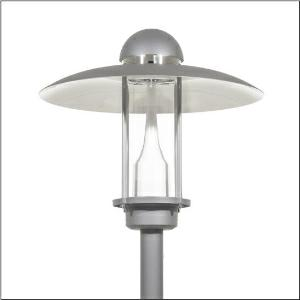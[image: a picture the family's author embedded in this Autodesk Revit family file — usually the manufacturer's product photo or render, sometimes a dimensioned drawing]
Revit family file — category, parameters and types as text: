
# Revit family: city-light_elegance_iq___pl1_2s_5xa5265of14h_1bea
name_source: partatom
category: Lighting Fixtures
units: mm (PartAtom-declared; Revit-internal decimal feet)

## family parameters
Cut with Voids When Loaded = No
Host = Face
Light Source = No
Part Type = Normal
Room Calculation Point = No
Round Connector Dimension = Use Diameter
Shared = No

## types (1)
- --- (1 x LED, 2840 lm, 21.8 W, 2700K)
    Apparent Load = 22 VA
    CIE Flux Codes = 24 63 94 98 100
    Color Rendering = 70
    Color Temperature = 2700K
    Default Elevation = 1800 mm
    Description = City-Light Elegance iQ, mast luminaire, Module 540 iQ-SR, primary light control with 3 zone facetted reflector, of plastic, silver coated, highly specular, structured, primary optical cover: cover, of PMMA, transparent, light distribution: PL1.2s, light emission: direct distribution, primary light characteristic: symmetric, installation type: post-top, LED, High Power LED, rated luminous flux: 2.840lm, luminous efficacy: 130lm/W, light colour: 727, colour temperature: 2700K, control gear: ECG iQ, control: presetting dimming logarithmic, Street-Remote, Auto-Match, Temp-Guard, Lumen-Switch, Night-Set, Smart-Wire, Light-Fading, Desk-Remote (wireless, voltage-free reading and setting of iQ features in the workshop via application-optimized NFC function/RFID function), optimised constant luminous flux control (CLO 2.0), with terminal, 6-pole, max. 2.5mm², mains connection: 230..240V, AC, 50/60Hz, start of lifetime: 22W, end of service life: 23W, reduction: 11W, luminaire housing, upper part, of aluminium, coated, Siteco® metallic grey (DB 702S), diameter: 750mm, height: 675mm, spigot size: d x l = 76 x 70mm (post-top) | with reducer (optional accessory) 60 x 70mm, post-top mast mounting element, of diecast aluminium, coated, Siteco® metallic grey (DB 702S), Module 540 iQ-SR, traffic white (RAL 9016), equipment: standard, protection rating (complete): IP65, insulation class (complete): insulation class II (safety insulation), certification: CE, ENEC, VDE, packaging unit: 1 piece

Light Distribution: PL1.2s
    Height = 675 mm
    Lamp = 1 x LED
    Lamp Light Flux = 2840 lm
    Lamp Power = 21.8 W
    Lamp count = 1
    Length = 750 mm
    Luminous efficacy = 130 lm/W
    Manufacturer = Siteco
    ModVariant = No
    Model = 5XA5265OF14H
    Number of Poles = 1
    OnlyDefault = Yes
    Power Factor = 1
    Product Name = City-Light Elegance iQ | PL1.2s
    Product group = mast luminaire | pylon top
    ProductGroupID = 6100
    Protection Class = Protection class II
    Protection Degree = IP 65
    RLX_Detail_Level = 1
    RLX_Emergency_Light_Flux = 0 lm
    RLX_Emergency_Type = 0
    RLX_Emergency_Type_DB = No
    RlxData = <blob elided: 72449 chars, md5=5f4786b8>
    Socket = socket
    Standby Power = 0 W
    System Light Flux = 2840 lm
    System Power = 22 W
    Type Comments = factory setting: luminous flux: 100 % | dim-lin: 254 | 456 mA
    Type Image = l_1006912.jpg
    URL = http://relux.com
    VarID = @adj_094835
    Voltage = 0 V
    Weight = 0.00 kg
    Width = 0 mm  [stored 0 ft]

note: [stored X ft] marks values corroborated as IEEE doubles in the binary element streams (Revit-internal decimal feet)

## geometry (parser evidence)
native form markers: Blend x4, Sweep x11
no freeform markers — native parametric forms only
